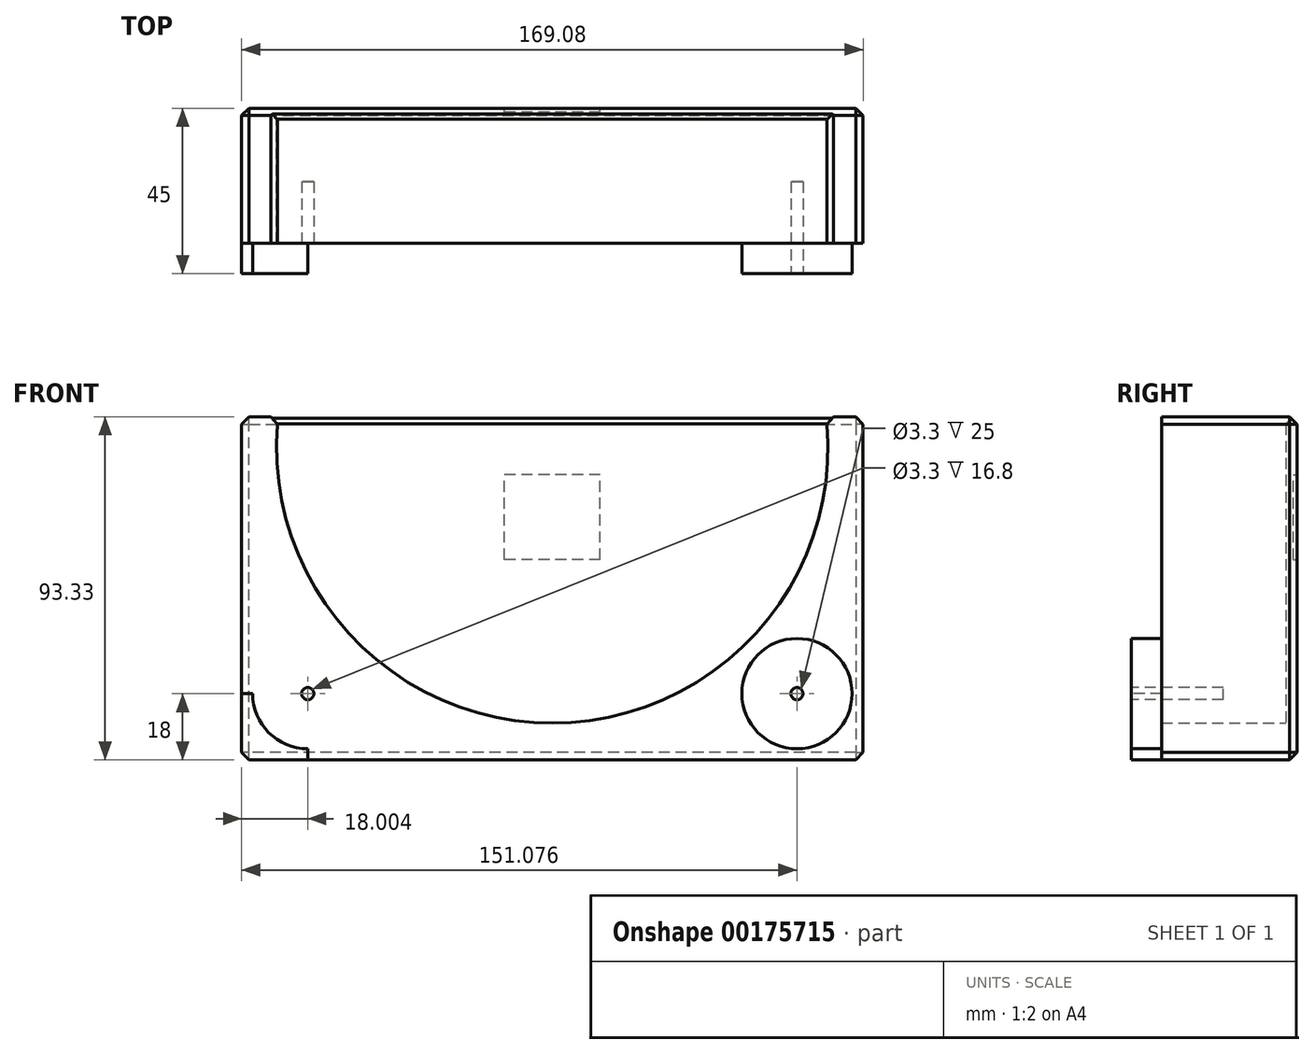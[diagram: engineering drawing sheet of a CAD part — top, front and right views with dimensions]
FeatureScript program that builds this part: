
annotation { "Feature Type Name" : "Feature", "Feature Type Description" : "" }
export const myFeature = defineFeature(function(context is Context, id is Id, definition is map)
    precondition{}
    {
        {
            var Q0;
            Q0=qCreatedBy(makeId("Front.planeOp"),FACE);
            var sketch = newSketch(context, id + "F0", { "sketchPlane" : qUnion([Q0])});
            skCircle(sketch, "E0", {"center": v(0, 85) * mm, "radius": 75 * mm});
            skLineSegment(sketch, "E1", {"start": v(-74.54, 93.33) * mm, "end": v(-84.54, 93.33) * mm});
            skLineSegment(sketch, "E2", {"start": v(-84.54, 93.33) * mm, "end": v(-84.54, 0) * mm});
            skLineSegment(sketch, "E3", {"start": v(-84.54, 0) * mm, "end": v(0, 0) * mm});
            skLineSegment(sketch, "E4.MirrorCS", {"start": v(74.54, 93.33) * mm, "end": v(84.54, 93.33) * mm});
            skLineSegment(sketch, "E5.MirrorCS", {"start": v(84.54, 93.33) * mm, "end": v(84.54, 0) * mm});
            skLineSegment(sketch, "E6.MirrorCS", {"start": v(84.54, 0) * mm, "end": v(0, 0) * mm});
            skLineSegment(sketch, "E7", {"start": v(74.54, 93.33) * mm, "end": v(-74.54, 93.33) * mm});
            skLineSegment(sketch, "E8", {"start": v(0, 54.53) * mm, "end": v(13, 54.53) * mm});
            skLineSegment(sketch, "E9", {"start": v(13, 54.53) * mm, "end": v(13, 77.53) * mm});
            skLineSegment(sketch, "E10", {"start": v(13, 77.53) * mm, "end": v(0, 77.53) * mm});
            skLineSegment(sketch, "E11", {"start": v(0, 77.53) * mm, "end": v(0, 65.32) * mm});
            skLineSegment(sketch, "E12.MirrorCS", {"start": v(-13, 77.53) * mm, "end": v(0, 77.53) * mm});
            skLineSegment(sketch, "E13.MirrorCS", {"start": v(-13, 54.53) * mm, "end": v(-13, 77.53) * mm});
            skLineSegment(sketch, "E14.MirrorCS", {"start": v(0, 54.53) * mm, "end": v(-13, 54.53) * mm});
            skLineSegment(sketch, "E15", {"start": v(0, 77.53) * mm, "end": v(0, 93.33) * mm});
            skSolve(sketch);
        }
        {
            var Q0;
            {var subQ0=sQuery(id+"F0.wireOp",EDGE,"E1");Q0=makeQuery(id+"F0.imprint","IMPRINT",FACE,{"disambiguationData":[TD([[makeQuery(id+"F0.imprint","IMPRINT",EDGE,{"derivedFrom":subQ0}),1.0]])]});}
            extrude(context, id + "F1", {"entities" : qUnion([Q0]), "depth" : 45 * mm});
        }
        {
            var Q0;
            Q0=makeQuery(id+"F1.opExtrude","CAP_FACE",FACE,{"disambiguationData":[OSD([sQuery(id+"F0.wireOp",EDGE,"E0"),sQuery(id+"F0.wireOp",EDGE,"E1"),sQuery(id+"F0.wireOp",EDGE,"E2"),sQuery(id+"F0.wireOp",EDGE,"E3"),sQuery(id+"F0.wireOp",EDGE,"E4.MirrorCS"),sQuery(id+"F0.wireOp",EDGE,"E5.MirrorCS"),sQuery(id+"F0.wireOp",EDGE,"E6.MirrorCS")])],"isStart":false});
            var sketch = newSketch(context, id + "F2", { "sketchPlane" : qUnion([Q0])});
            skLineSegment(sketch, "E16", {"start": v(-84.54, 93.33) * mm, "end": v(84.54, 93.33) * mm});
            skLineSegment(sketch, "E17", {"start": v(84.54, 93.33) * mm, "end": v(84.54, 0) * mm});
            skLineSegment(sketch, "E18", {"start": v(84.54, 0) * mm, "end": v(-84.54, 0) * mm});
            skLineSegment(sketch, "E19", {"start": v(-84.54, 0) * mm, "end": v(-84.54, 93.33) * mm});
            skLineSegment(sketch, "E20", {"start": v(-84.54, 18) * mm, "end": v(-66.54, 18) * mm});
            skLineSegment(sketch, "E21", {"start": v(-66.54, 18) * mm, "end": v(-66.54, 0) * mm});
            skCircle(sketch, "E22", {"center": v(-66.54, 18) * mm, "radius": 15 * mm});
            skLineSegment(sketch, "E23", {"start": v(0, 0) * mm, "end": v(0, 4.98) * mm});
            skCircle(sketch, "E24.MirrorC", {"center": v(66.54, 18) * mm, "radius": 15 * mm});
            skCircle(sketch, "E25", {"center": v(-66.54, 18) * mm, "radius": 1.65 * mm});
            skCircle(sketch, "E26", {"center": v(66.54, 18) * mm, "radius": 1.65 * mm});
            skSolve(sketch);
        }
        {
            var Q0;
            {var subQ0=sQuery(id+"F0.wireOp",EDGE,"E7");Q0=makeQuery(id+"F0.imprint","IMPRINT",FACE,{"disambiguationData":[TD([[makeQuery(id+"F0.imprint","IMPRINT",EDGE,{"derivedFrom":subQ0}),1.0]])]});}
            var Q1;
            Q1=makeQuery(id+"F0.imprint","IMPRINT",FACE,{"disambiguationData":[TD([[makeQuery(id+"F0.imprint","IMPRINT",EDGE,{"derivedFrom":sQuery(id+"F0.wireOp",EDGE,"E8")}),1.0]])]});
            extrude(context, id + "F3", {"entities" : qUnion([Q0, Q1]), "operationType" : NewBodyOperationType.ADD, "depth" : 3 * mm});
        }
        {
            var Q0;
            {var subQ1=makeQuery(id+"F1.opExtrude","CAP_EDGE",EDGE,{"disambiguationData":[OSD([sQuery(id+"F0.wireOp",EDGE,"E0")])],"isStart":false});Q0=makeQuery(id+"F2.imprint","IMPRINT",FACE,{"disambiguationData":[TD([[makeQuery(id+"F2.imprint","IMPRINT",EDGE,{"derivedFrom":subQ1}),1.0]])]});}
            var Q1;
            Q1=makeQuery(id+"F2.imprint","IMPRINT",FACE,{"disambiguationData":[TD([[makeQuery(id+"F2.imprint","IMPRINT",EDGE,{"derivedFrom":sQuery(id+"F2.wireOp",EDGE,"E24.MirrorC")}),-1.0]])]});
            var Q2;
            {var subQ0=sQuery(id+"F2.wireOp",EDGE,"E22");var subQ1=sQuery(id+"F2.wireOp",EDGE,"E20");var subQ2=makeQuery(id+"F2.imprint","INTERSECT",VERTEX,{"derivedFrom":[subQ1,subQ0]});Q2=makeQuery(id+"F2.imprint","IMPRINT",FACE,{"disambiguationData":[TD([[makeQuery(id+"F2.imprint","IMPRINT",EDGE,{"disambiguationData":[TD([[subQ2,-1.0]])],"derivedFrom":subQ1}),1.0]])]});}
            var Q3;
            {var subQ0=sQuery(id+"F2.wireOp",EDGE,"E22");var subQ1=sQuery(id+"F2.wireOp",EDGE,"E20");var subQ2=makeQuery(id+"F2.imprint","INTERSECT",VERTEX,{"derivedFrom":[subQ1,subQ0]});Q3=makeQuery(id+"F2.imprint","IMPRINT",FACE,{"disambiguationData":[TD([[makeQuery(id+"F2.imprint","IMPRINT",EDGE,{"disambiguationData":[TD([[subQ2,-1.0]])],"derivedFrom":subQ1}),-1.0]])]});}
            extrude(context, id + "F4", {"entities" : qUnion([Q0, Q1, Q2, Q3]), "operationType" : NewBodyOperationType.REMOVE, "oppositeDirection" : true, "depth" : 8.2 * mm});
        }
        {
            var Q0;
            Q0=makeQuery(id+"F2.imprint","IMPRINT",FACE,{"disambiguationData":[TD([[makeQuery(id+"F2.imprint","IMPRINT",EDGE,{"derivedFrom":sQuery(id+"F2.wireOp",EDGE,"E26")}),1.0]])]});
            var Q1;
            {var subQ0=sQuery(id+"F2.wireOp",EDGE,"E21");var subQ1=sQuery(id+"F2.wireOp",EDGE,"E20");var subQ2=makeQuery(id+"F2.imprint","INTERSECT",VERTEX,{"derivedFrom":[subQ1,subQ0]});Q1=makeQuery(id+"F2.imprint","IMPRINT",FACE,{"disambiguationData":[TD([[makeQuery(id+"F2.imprint","IMPRINT",EDGE,{"disambiguationData":[TD([[subQ2,1.0]])],"derivedFrom":subQ1}),1.0]])]});}
            var Q2;
            {var subQ0=sQuery(id+"F2.wireOp",EDGE,"E21");var subQ1=sQuery(id+"F2.wireOp",EDGE,"E20");var subQ2=makeQuery(id+"F2.imprint","INTERSECT",VERTEX,{"derivedFrom":[subQ1,subQ0]});Q2=makeQuery(id+"F2.imprint","IMPRINT",FACE,{"disambiguationData":[TD([[makeQuery(id+"F2.imprint","IMPRINT",EDGE,{"disambiguationData":[TD([[subQ2,1.0]])],"derivedFrom":subQ1}),-1.0]])]});}
            var Q3;
            Q3=sQuery(id+"F2.wireOp",EDGE,"E26");
            var Q4;
            Q4=sQuery(id+"F2.wireOp",EDGE,"E25");
            extrude(context, id + "F5", {"entities" : qUnion([Q0, Q1, Q2]), "operationType" : NewBodyOperationType.REMOVE, "surfaceEntities" : qUnion([Q3, Q4]), "oppositeDirection" : true, "depth" : 25 * mm});
        }
        {
            var Q0;
            Q0=makeQuery(id+"F0.imprint","IMPRINT",FACE,{"disambiguationData":[TD([[makeQuery(id+"F0.imprint","IMPRINT",EDGE,{"derivedFrom":sQuery(id+"F0.wireOp",EDGE,"E8")}),1.0]])]});
            extrude(context, id + "F6", {"entities" : qUnion([Q0]), "operationType" : NewBodyOperationType.REMOVE, "depth" : 1 * mm});
        }
        {
            var Q0;
            Q0=makeQuery(id+"F1.opExtrude","SWEPT_EDGE",EDGE,{"disambiguationData":[OSD([sQuery(id+"F0.wireOp",EDGE,"E0"),sQuery(id+"F0.wireOp",EDGE,"E1"),sQuery(id+"F0.wireOp",EDGE,"E7")])]});
            var Q1;
            Q1=makeQuery(id+"F3.boolean.opBoolean","MERGE",EDGE,{"derivedFrom":[makeQuery(id+"F1.opExtrude","CAP_EDGE",EDGE,{"disambiguationData":[OSD([sQuery(id+"F0.wireOp",EDGE,"E1")])],"isStart":true}),makeQuery(id+"F1.opExtrude","CAP_EDGE",EDGE,{"disambiguationData":[OSD([sQuery(id+"F0.wireOp",EDGE,"E4.MirrorCS")])],"isStart":true}),makeQuery(id+"F3.opExtrude","CAP_EDGE",EDGE,{"disambiguationData":[OSD([sQuery(id+"F0.wireOp",EDGE,"E7")])],"isStart":true})]});
            var Q2;
            Q2=makeQuery(id+"F3.opExtrude","CAP_EDGE",EDGE,{"disambiguationData":[OSD([sQuery(id+"F0.wireOp",EDGE,"E7")])],"isStart":false});
            var Q3;
            Q3=makeQuery(id+"F1.opExtrude","CAP_EDGE",EDGE,{"disambiguationData":[OSD([sQuery(id+"F0.wireOp",EDGE,"E2")])],"isStart":true});
            var Q4;
            Q4=makeQuery(id+"F1.opExtrude","CAP_EDGE",EDGE,{"disambiguationData":[OSD([sQuery(id+"F0.wireOp",EDGE,"E5.MirrorCS")])],"isStart":true});
            var Q5;
            Q5=makeQuery(id+"F1.opExtrude","SWEPT_EDGE",EDGE,{"disambiguationData":[OSD([sQuery(id+"F0.wireOp",EDGE,"E4.MirrorCS"),sQuery(id+"F0.wireOp",EDGE,"E5.MirrorCS")])]});
            var Q6;
            Q6=makeQuery(id+"F1.opExtrude","SWEPT_EDGE",EDGE,{"disambiguationData":[OSD([sQuery(id+"F0.wireOp",EDGE,"E0"),sQuery(id+"F0.wireOp",EDGE,"E4.MirrorCS"),sQuery(id+"F0.wireOp",EDGE,"E7")])]});
            var Q7;
            Q7=makeQuery(id+"F1.opExtrude","SWEPT_EDGE",EDGE,{"disambiguationData":[OSD([sQuery(id+"F0.wireOp",EDGE,"E1"),sQuery(id+"F0.wireOp",EDGE,"E2")])]});
            var Q8;
            Q8=makeQuery(id+"F1.opExtrude","SWEPT_EDGE",EDGE,{"disambiguationData":[OSD([sQuery(id+"F0.wireOp",EDGE,"E2"),sQuery(id+"F0.wireOp",EDGE,"E3")])]});
            var Q9;
            Q9=makeQuery(id+"F1.opExtrude","CAP_EDGE",EDGE,{"disambiguationData":[OSD([sQuery(id+"F0.wireOp",EDGE,"E3"),sQuery(id+"F0.wireOp",EDGE,"E6.MirrorCS")])],"isStart":true});
            var Q10;
            Q10=makeQuery(id+"F1.opExtrude","SWEPT_EDGE",EDGE,{"disambiguationData":[OSD([sQuery(id+"F0.wireOp",EDGE,"E5.MirrorCS"),sQuery(id+"F0.wireOp",EDGE,"E6.MirrorCS")])]});
            chamfer(context, id + "F7", {"entities" : qUnion([Q0, Q1, Q2, Q3, Q4, Q5, Q6, Q7, Q8, Q9, Q10]), "width" : 2 * mm, "tangentPropagation" : true});
        }
    });
